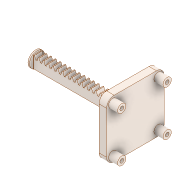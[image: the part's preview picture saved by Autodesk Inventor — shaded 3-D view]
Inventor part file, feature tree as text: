
AUTODESK INVENTOR PART (.ipt)
format: ipt  version: 2020 (Build 240168000, 168)  size: 272,384 bytes
history: mixed  units: mm
features: extrude x4, sketch x3, fillet x1, other x1, imported_body x1
ambient origin geometry x8: Origin, YZ Plane, XZ Plane, XY Plane, X Axis, Y Axis, Z Axis, Center Point
bodies: Solid1 (imported_parasolid)
feature tree (10):
  extrude  "Extrusion1"  Depth=38.0mm
  extrude  "Extrusion2"  Depth=5.0mm TaperAngle=0.0deg
  extrude  "Extrusion3"  Depth=5.0mm
  extrude  "Extrusion4"  Depth=5.0mm
  fillet  "Fillet1"  Radius=2.5mm
  sketch  "Sketch1"  dims[d0=5.0mm d1=0.0mm d2=38.0mm]
  sketch  "Sketch3"  dims[d3=38.0mm d4=5.0mm d5=0.0mm]
  sketch  "Sketch4"  dims[d6=2.5mm d7=2.5mm d8=2.5mm d9=2.5mm d10=4.0mm d11=4.0mm d12=5.0mm d13=0.0mm d14=5.5mm d15=5.5mm d16=5.5mm d17=5.5mm d18=6.0mm d19=0.0mm d20=5.0mm]
  other  "Boss-Extrude6"
  imported_body  NMx_Import_Brep_tag  [imported B-rep: ~151 faces, bbox_mm=[72.0, 38.0, 38.0]]
